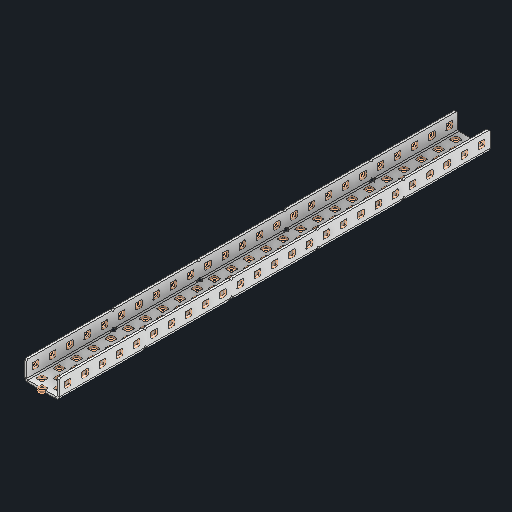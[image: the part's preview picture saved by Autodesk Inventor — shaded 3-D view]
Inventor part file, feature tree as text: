
AUTODESK INVENTOR PART (.ipt)
format: ipt  version: 2024 (Build 280153000, 153)  size: 2,036,736 bytes
history: native  units: in
note: dims shown in document units (in); Inventor stores cm internally (conversion verified against a paired STEP export)
features: other x256, sketch x5, sheet_metal_op x1
ambient origin geometry x8: Origin, YZ Plane, XZ Plane, XY Plane, X Axis, Y Axis, Z Axis, Center Point
bodies: Solid1 (feature_tree)
feature tree (262):
  other  "Alu C 1x2x1x25.ipt"
  other  "Solid1::Alu C 1x2x1x25.ipt"
  other  "TaggingFeature1"
  sketch  "Sketch1"  dims[d0=0.3937in]
  sketch  "Sketch2"  dims[d1=0.0625in]
  sketch  "Sketch3"
  other  "Flange Pattern Sketch"
  sketch  "Sketch9"
  sheet_metal_op  "Body Pattern Sketch"
  other  "Arc Length"
  sketch  "Sketch14"
  other  "Flange Pattern Plane"
  other  "Srf1"
  other  "Srf2"
  other  "Srf3"
  other  "Srf4"
  other  "Srf5"
  other  "Srf6"
  other  "Srf7"
  other  "Srf8"
  other  "Srf9"
  other  "Srf10"
  other  "Srf11"
  other  "Srf12"
  other  "Srf13"
  other  "Srf14"
  other  "Srf15"
  other  "Srf16"
  other  "Srf17"
  other  "Srf18"
  other  "Srf19"
  other  "Srf20"
  other  "Srf21"
  other  "Srf22"
  other  "Srf23"
  other  "Srf24"
  other  "Srf25"
  other  "Srf26"
  other  "Srf27"
  other  "Srf28"
  other  "Srf29"
  other  "Srf30"
  other  "Srf31"
  other  "Srf32"
  other  "Srf33"
  other  "Srf34"
  other  "Srf35"
  other  "Srf36"
  other  "Srf37"
  other  "Srf38"
  other  "Srf39"
  other  "Srf40"
  other  "Srf41"
  other  "Srf42"
  other  "Srf43"
  other  "Srf44"
  other  "Srf45"
  other  "Srf46"
  other  "Srf47"
  other  "Srf48"
  other  "Srf49"
  other  "Srf50"
  other  "Srf51"
  other  "Srf52"
  other  "Srf53"
  other  "Srf54"
  other  "Srf55"
  other  "Srf56"
  other  "Srf57"
  other  "Srf58"
  other  "Srf59"
  other  "Srf60"
  other  "Srf61"
  other  "Srf62"
  other  "Srf63"
  other  "Srf64"
  other  "Srf65"
  other  "Srf66"
  other  "Srf67"
  other  "Srf68"
  other  "Srf69"
  other  "Srf70"
  other  "Srf71"
  other  "Srf72"
  other  "Srf73"
  other  "Srf74"
  other  "Srf75"
  other  "Srf76"
  other  "Srf77"
  other  "Srf78"
  other  "Srf79"
  other  "Srf80"
  other  "Srf81"
  other  "Srf82"
  other  "Srf83"
  other  "Srf84"
  other  "Srf85"
  other  "Srf86"
  other  "Srf87"
  other  "Srf88"
  other  "Srf89"
  other  "Srf90"
  other  "Srf91"
  other  "Srf92"
  other  "Srf93"
  other  "Srf94"
  other  "Srf95"
  other  "Srf96"
  other  "Srf97"
  other  "Srf98"
  other  "Srf99"
  other  "Srf100"
  other  "Srf101"
  other  "Srf102"
  other  "Srf103"
  other  "Srf104"
  other  "Srf105"
  other  "Srf106"
  other  "Srf107"
  other  "Srf108"
  other  "Srf109"
  other  "Srf110"
  other  "Srf111"
  other  "Srf112"
  other  "Srf113"
  other  "Srf114"
  other  "Srf115"
  other  "Srf116"
  other  "Srf117"
  other  "Srf118"
  other  "Srf119"
  other  "Srf120"
  other  "Srf121"
  other  "Srf122"
  other  "Srf123"
  other  "Srf124"
  other  "Srf125"
  other  "Srf1::Derived"
  other  "Srf2::Derived"
  other  "Srf823::Derived"
  other  "Srf824::Derived"
  other  "Srf825::Derived"
  other  "Srf826::Derived"
  other  "Srf827::Derived"
  other  "Srf828::Derived"
  other  "Srf829::Derived"
  other  "Srf922::Derived"
  other  "Srf923::Derived"
  other  "Srf924::Derived"
  other  "Srf925::Derived"
  other  "Srf926::Derived"
  other  "Srf1143::Derived"
  other  "Srf1144::Derived"
  other  "Srf1145::Derived"
  other  "Srf1146::Derived"
  other  "Srf1147::Derived"
  other  "Srf1148::Derived"
  other  "Srf1149::Derived"
  other  "Srf1150::Derived"
  other  "Srf1151::Derived"
  other  "Srf1152::Derived"
  other  "Srf1153::Derived"
  other  "Srf1154::Derived"
  other  "Srf1155::Derived"
  other  "Srf1156::Derived"
  other  "Srf1157::Derived"
  other  "Srf1158::Derived"
  other  "Srf1159::Derived"
  other  "Srf1160::Derived"
  other  "Srf1161::Derived"
  other  "Srf1162::Derived"
  other  "Srf1163::Derived"
  other  "Srf1164::Derived"
  other  "Srf1165::Derived"
  other  "Srf1166::Derived"
  other  "Srf1167::Derived"
  other  "Srf1168::Derived"
  other  "Srf1169::Derived"
  other  "Srf1170::Derived"
  other  "Srf1171::Derived"
  other  "Srf1172::Derived"
  other  "Srf1173::Derived"
  other  "Srf1174::Derived"
  other  "Srf1175::Derived"
  other  "Srf1176::Derived"
  other  "Srf1177::Derived"
  other  "Srf1178::Derived"
  other  "Srf91::Derived"
  other  "Srf92::Derived"
  other  "Srf856::Derived"
  other  "Srf857::Derived"
  other  "Srf858::Derived"
  other  "Srf859::Derived"
  other  "Srf860::Derived"
  other  "Srf861::Derived"
  other  "Srf862::Derived"
  other  "Srf959::Derived"
  other  "Srf960::Derived"
  other  "Srf961::Derived"
  other  "Srf962::Derived"
  other  "Srf963::Derived"
  other  "Srf1199::Derived"
  other  "Srf1200::Derived"
  other  "Srf1201::Derived"
  other  "Srf1202::Derived"
  other  "Srf1203::Derived"
  other  "Srf1204::Derived"
  other  "Srf1205::Derived"
  other  "Srf1206::Derived"
  other  "Srf1207::Derived"
  other  "Srf1208::Derived"
  other  "Srf1209::Derived"
  other  "Srf1210::Derived"
  other  "Srf1211::Derived"
  other  "Srf1212::Derived"
  other  "Srf1213::Derived"
  other  "Srf1214::Derived"
  other  "Srf1215::Derived"
  other  "Srf1216::Derived"
  other  "Srf1217::Derived"
  other  "Srf1218::Derived"
  other  "Srf1219::Derived"
  other  "Srf1220::Derived"
  other  "Srf1221::Derived"
  other  "Srf1222::Derived"
  other  "Srf1223::Derived"
  other  "Srf1224::Derived"
  other  "Srf1225::Derived"
  other  "Srf1226::Derived"
  other  "Srf1227::Derived"
  other  "Srf1228::Derived"
  other  "Srf1229::Derived"
  other  "Srf1230::Derived"
  other  "Srf1231::Derived"
  other  "Srf1232::Derived"
  other  "Srf1233::Derived"
  other  "Srf1234::Derived"
  other  "Srf786::Derived"
  other  "Srf889::Derived"
  other  "Srf890::Derived"
  other  "Srf891::Derived"
  other  "Srf892::Derived"
  other  "Srf893::Derived"
  other  "Srf894::Derived"
  other  "Srf895::Derived"
  other  "Srf896::Derived"
  other  "Srf996::Derived"
  other  "Srf997::Derived"
  other  "Srf998::Derived"
  other  "Srf999::Derived"
  other  "Srf1000::Derived"
  other  "Srf1255::Derived"
  other  "Srf1256::Derived"
  other  "Srf1257::Derived"
  other  "Srf1258::Derived"
  other  "Srf1259::Derived"
  other  "Srf1260::Derived"
  other  "Srf1261::Derived"
  other  "Srf1262::Derived"
  other  "Srf1263::Derived"
  other  "Srf1264::Derived"
  other  "Srf1265::Derived"
